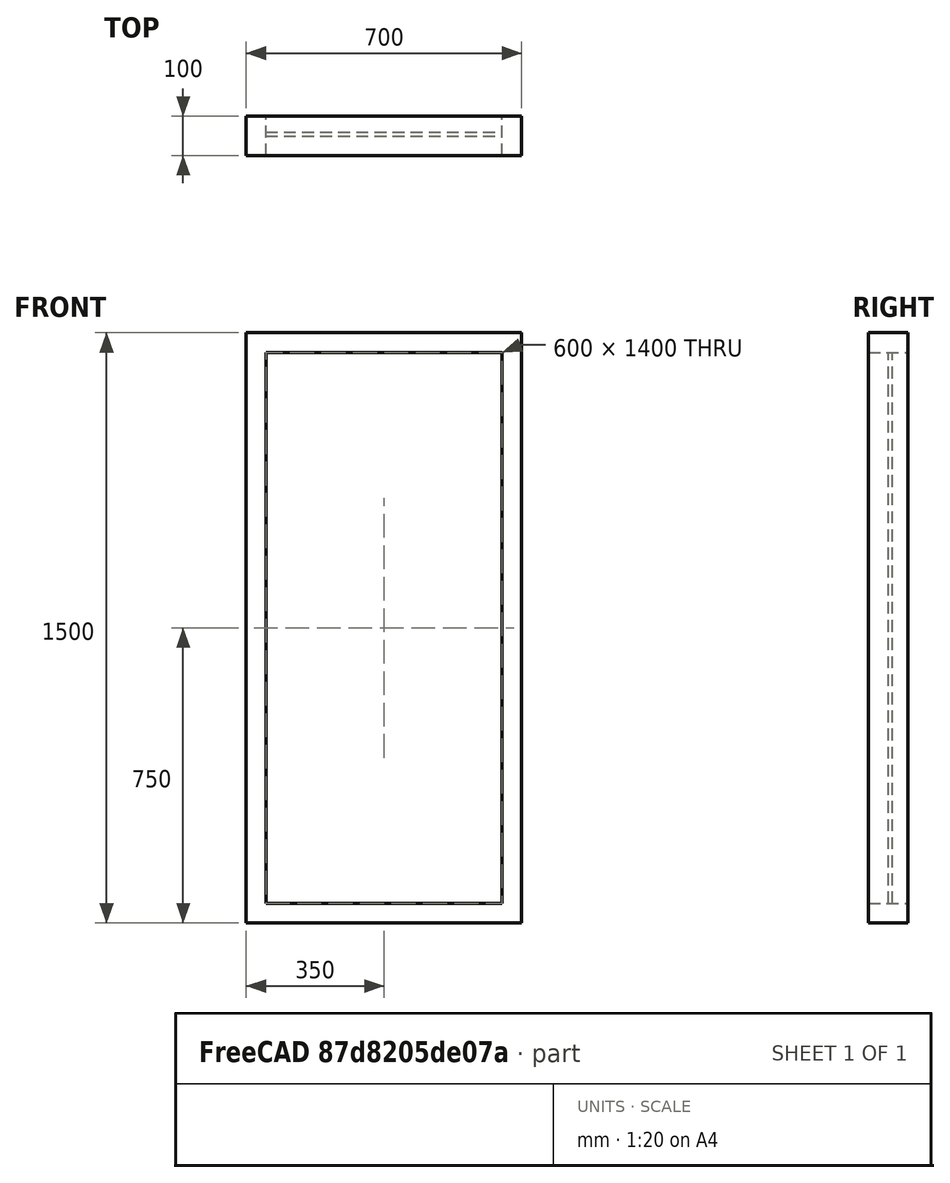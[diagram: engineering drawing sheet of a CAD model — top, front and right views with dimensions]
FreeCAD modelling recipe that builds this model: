
FCSTD DOCUMENT  (FreeCAD 0.19R)
Label: simple_window
License: Creative Commons Attribution-ShareAlike
LicenseURL: http://creativecommons.org/licenses/by-sa/4.0/
objects: Sketcher::SketchObject×1, Part::FeaturePython×1
note: 2 computed .brp shape members not serialized (recipe doc carries the construction recipe); baked Part::Feature solids carry a one-line shape summary decoded from their .brp

FEATURE [Sketcher::SketchObject] Sketch
  FullyConstrained = true
  Placement = pos=(0,0,0) rot=(1,0,0;1.5708rad)
  sketch-geometry (8):
    g0: LineSegment StartX=0 StartY=0 StartZ=0 EndX=700 EndY=0 EndZ=0
    g1: LineSegment StartX=700 StartY=0 StartZ=0 EndX=700 EndY=1500 EndZ=0
    g2: LineSegment StartX=700 StartY=1500 StartZ=0 EndX=0 EndY=1500 EndZ=0
    g3: LineSegment StartX=0 StartY=1500 StartZ=0 EndX=0 EndY=0 EndZ=0
    g4: LineSegment StartX=50 StartY=50 StartZ=0 EndX=650 EndY=50 EndZ=0
    g5: LineSegment StartX=650 StartY=50 StartZ=0 EndX=650 EndY=1450 EndZ=0
    g6: LineSegment StartX=650 StartY=1450 StartZ=0 EndX=50 EndY=1450 EndZ=0
    g7: LineSegment StartX=50 StartY=1450 StartZ=0 EndX=50 EndY=50 EndZ=0
  constraints (23):
    c: Coincident(g0,g1)
    c: Coincident(g1,g2)
    c: Coincident(g2,g3)
    c: Coincident(g3,g0)
    c: Horizontal(g0)
    c: Horizontal(g2)
    c: Vertical(g1)
    c: Vertical(g3)
    c: Coincident(g4,g5)
    c: Coincident(g5,g6)
    c: Coincident(g6,g7)
    c: Coincident(g7,g4)
    c: Horizontal(g4)
    c: Horizontal(g6)
    c: Vertical(g5)
    c: Vertical(g7)
    c: DistanceY(g1) = 1500  'Height'
    c: DistanceX(g0) = 700  'Width'
    c: DistanceY(g6,g2) = 50  'Frame1'
    c: DistanceX(g2,g6) = 50  'Frame2'
    c: DistanceX(g4,g0) = 50  'Frame3'
    c: DistanceY(g0,g4) = 50  'Frame4'
    c: Coincident(g0,g-1)
FEATURE [Part::FeaturePython] Window  # Arch/BIM 170 (typed FeaturePython)
  Area = 1050000
  Base = -> Sketch
  Frame = 50
  Height = 1500
  HoleDepth = 0
  HoleWire = 0
  HorizontalArea = 0
  IfcData = attributes={"GlobalId": {"name": "GlobalId", "type": "IfcGloballyUniqueId", "is_enum": false, "enum_values": []}, "Description": {"... (+1230 chars omitted),+1 more (map truncated)
  IfcType = 170
  LouvreSpacing = 0
  LouvreWidth = 0
  MoveBase = false
  MoveWithHost = true
  Normal = (0,1,-2e-16)
  Opening = 0
  OverallHeight = 1500
  OverallWidth = 700
  PartitioningType = 0
  PerimeterLength = 0
  PredefinedType = 0
  Preset = 1
  SymbolElevation = false
  SymbolPlan = false
  VerticalArea = 0
  Width = 700
  WindowParts = OuterFrame | Frame | Wire0,Wire1 | 50.0+V | 0.00+V | Glass | Glass panel | Wire1 | 10.0 | 50.0+V
  expr: OverallHeight = .Height.Value
  expr: OverallWidth = .Width.Value
